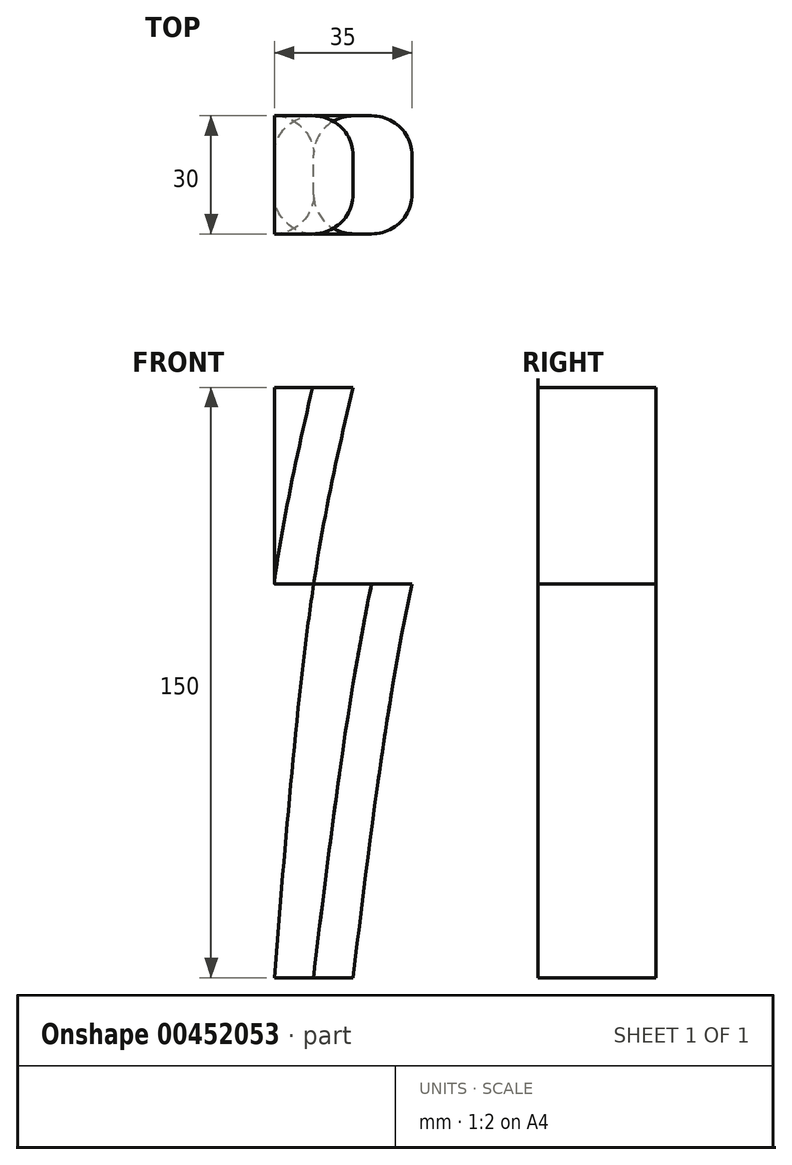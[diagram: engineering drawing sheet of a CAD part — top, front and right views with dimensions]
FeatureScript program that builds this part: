
annotation { "Feature Type Name" : "Feature", "Feature Type Description" : "" }
export const myFeature = defineFeature(function(context is Context, id is Id, definition is map)
    precondition{}
    {
        {
            var Q0;
            Q0=qCreatedBy(makeId("Front.planeOp"),FACE);
            var sketch = newSketch(context, id + "F0", { "sketchPlane" : qUnion([Q0])});
            skLineSegment(sketch, "E0", {"start": v(0, 26) * mm, "end": v(0, 176) * mm});
            skLineSegment(sketch, "E1", {"start": v(0, 176) * mm, "end": v(50, 176) * mm});
            skLineSegment(sketch, "E2", {"start": v(0, 176) * mm, "end": v(20, 176) * mm});
            skLineSegment(sketch, "E3", {"start": v(0, 26) * mm, "end": v(0, 101) * mm});
            skLineSegment(sketch, "E4", {"start": v(0, 101) * mm, "end": v(10, 101) * mm});
            skLineSegment(sketch, "E5", {"start": v(0, 26) * mm, "end": v(0, 126) * mm});
            skLineSegment(sketch, "E6", {"start": v(0, 126) * mm, "end": v(10, 126) * mm});
            skFitSpline(sketch, "E7", {"points": [v(0, 26) * mm, v(10, 126) * mm, v(20, 176) * mm], "startDerivative": vector(15.1, 186.13) * mm, "endDerivative": vector(25.48, 109.58) * mm});
            skLineSegment(sketch, "E8", {"start": v(10, 126) * mm, "end": v(30, 126) * mm});
            skLineSegment(sketch, "E9", {"start": v(10, 26) * mm, "end": v(20, 26) * mm});
            skLineSegment(sketch, "E10", {"start": v(30, 126) * mm, "end": v(35, 126) * mm});
            skFitSpline(sketch, "E11", {"points": [v(20, 26) * mm, v(35, 126) * mm, v(50, 176) * mm], "startDerivative": vector(22.84, 187.06) * mm, "endDerivative": vector(37.99, 108.66) * mm});
            skLineSegment(sketch, "E12", {"start": v(10, 26) * mm, "end": v(0, 26) * mm});
            skSolve(sketch);
        }
        {
            var Q0;
            {var subQ1=sQuery(id+"F0.wireOp",EDGE,"E1");Q0=makeQuery(id+"F0.imprint","IMPRINT",FACE,{"disambiguationData":[TD([[makeQuery(id+"F0.imprint","IMPRINT",EDGE,{"derivedFrom":subQ1}),-1.0]])]});}
            var Q1;
            {var subQ1=sQuery(id+"F0.wireOp",EDGE,"E8");Q1=makeQuery(id+"F0.imprint","IMPRINT",FACE,{"disambiguationData":[TD([[makeQuery(id+"F0.imprint","IMPRINT",EDGE,{"derivedFrom":subQ1}),-1.0]])]});}
            extrude(context, id + "F1", {"entities" : qUnion([Q0, Q1]), "depth" : 15 * mm, "hasSecondDirection" : true, "secondDirectionOppositeDirection" : true, "secondDirectionDepth" : 15 * mm});
        }
        {
            var Q0;
            Q0=makeQuery(id+"F1.opExtrude","CAP_EDGE",EDGE,{"disambiguationData":[OSD([sQuery(id+"F0.wireOp",EDGE,"E7")])],"isStart":false});
            var Q1;
            Q1=makeQuery(id+"F1.opExtrude","CAP_EDGE",EDGE,{"disambiguationData":[OSD([sQuery(id+"F0.wireOp",EDGE,"E11")])],"isStart":false});
            var Q2;
            Q2=makeQuery(id+"F1.opExtrude","CAP_EDGE",EDGE,{"disambiguationData":[OSD([sQuery(id+"F0.wireOp",EDGE,"E7")])],"isStart":true});
            var Q3;
            Q3=makeQuery(id+"F1.opExtrude","CAP_EDGE",EDGE,{"disambiguationData":[OSD([sQuery(id+"F0.wireOp",EDGE,"E11")])],"isStart":true});
            fillet(context, id + "F2", {"entities" : qUnion([Q0, Q1, Q2, Q3]), "radius" : 10 * mm, "tangentPropagation" : true, "allowEdgeOverflow" : false});
        }
    });
